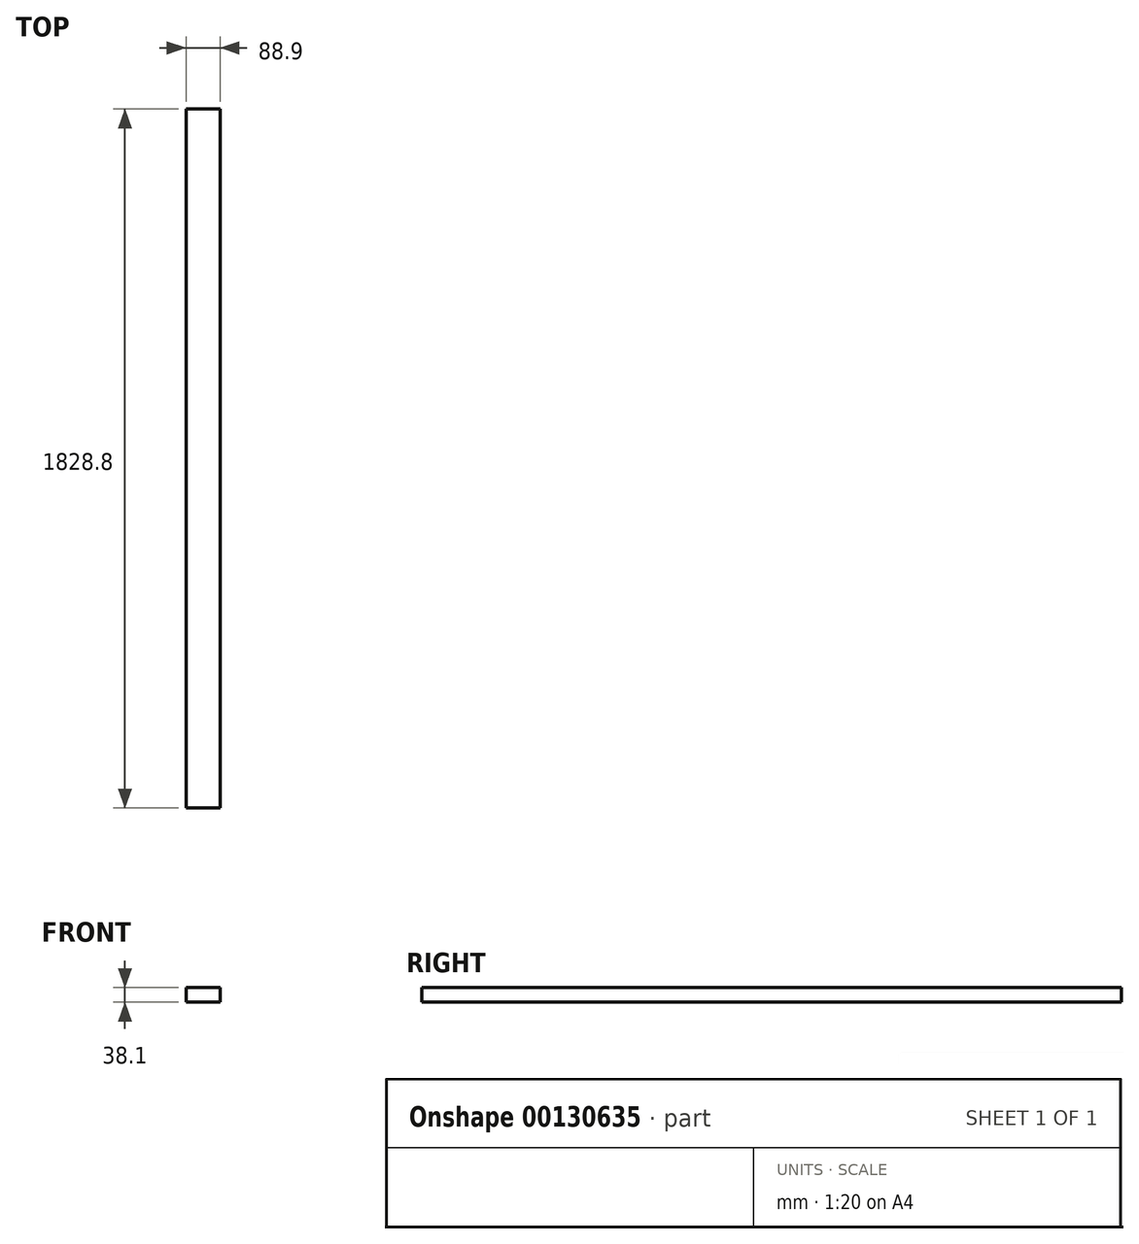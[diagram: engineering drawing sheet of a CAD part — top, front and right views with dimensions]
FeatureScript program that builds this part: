
annotation { "Feature Type Name" : "Feature", "Feature Type Description" : "" }
export const myFeature = defineFeature(function(context is Context, id is Id, definition is map)
    precondition{}
    {
        {
            var Q0;
            Q0=qCreatedBy(makeId("Top.planeOp"),FACE);
            var sketch = newSketch(context, id + "F0", { "sketchPlane" : qUnion([Q0])});
            skLineSegment(sketch, "E0.bottom", {"start": v(0, 0) * mm, "end": v(88.9, 0) * mm});
            skLineSegment(sketch, "E0.top", {"start": v(0, 1828.8) * mm, "end": v(88.9, 1828.8) * mm});
            skLineSegment(sketch, "E0.left", {"start": v(0, 0) * mm, "end": v(0, 1828.8) * mm});
            skLineSegment(sketch, "E0.right", {"start": v(88.9, 0) * mm, "end": v(88.9, 1828.8) * mm});
            skSolve(sketch);
        }
        {
            var Q0;
            Q0=makeQuery(id+"F0.imprint","IMPRINT",FACE,{"disambiguationData":[TD([[makeQuery(id+"F0.imprint","IMPRINT",EDGE,{"derivedFrom":sQuery(id+"F0.wireOp",EDGE,"E0.bottom")}),1.0]])]});
            extrude(context, id + "F1", {"entities" : qUnion([Q0]), "depth" : 38.1 * mm});
        }
    });
